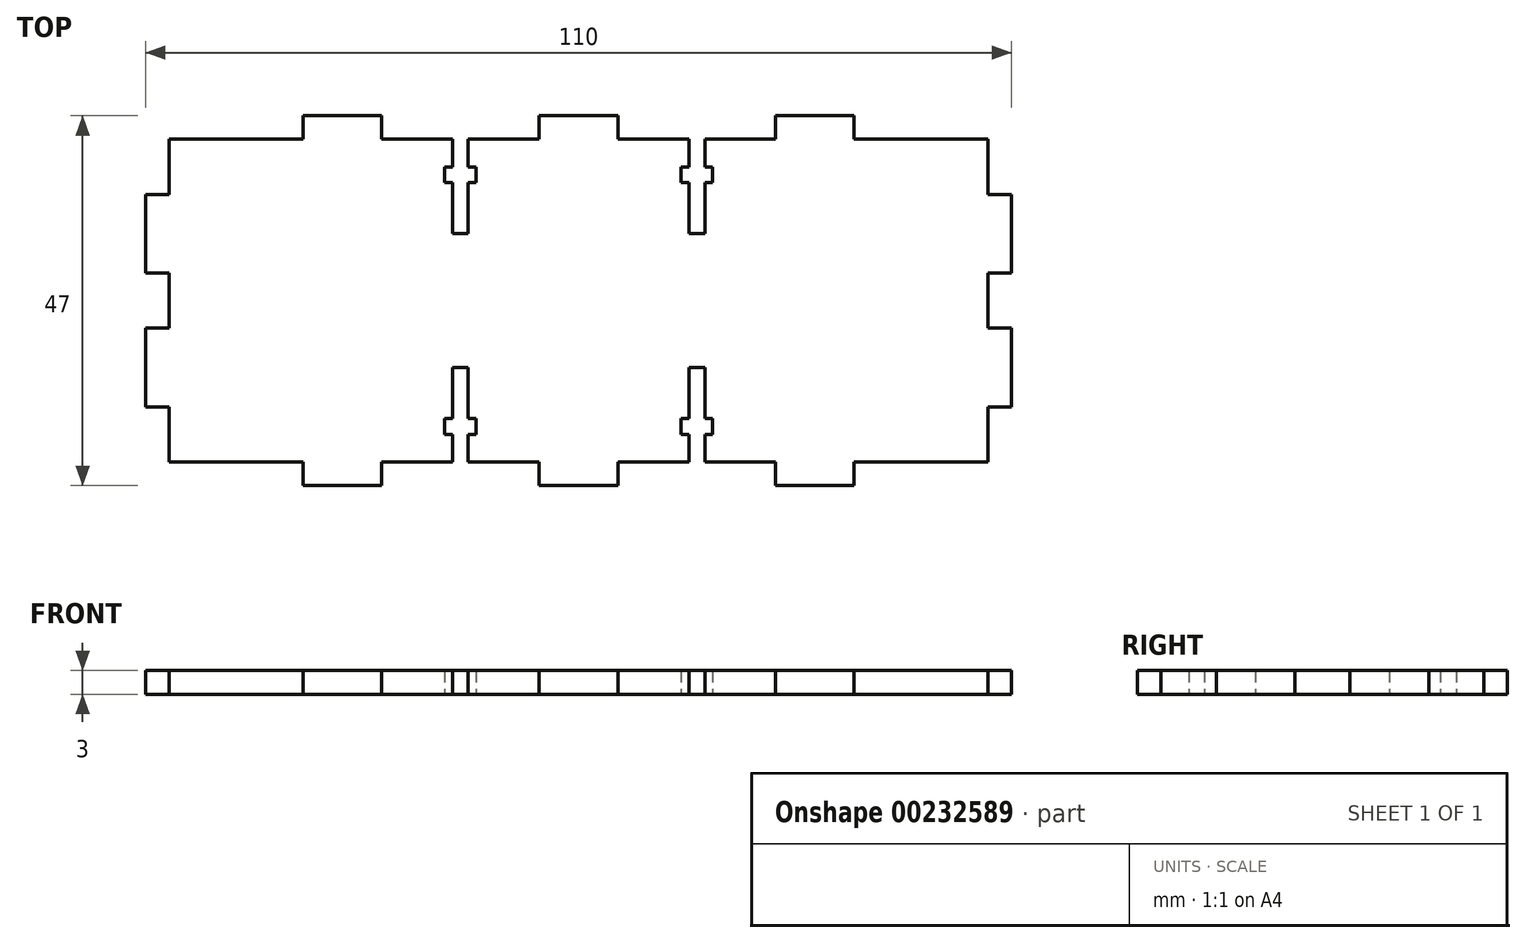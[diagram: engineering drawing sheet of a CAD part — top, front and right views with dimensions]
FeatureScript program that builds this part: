
annotation { "Feature Type Name" : "Feature", "Feature Type Description" : "" }
export const myFeature = defineFeature(function(context is Context, id is Id, definition is map)
    precondition{}
    {
        {
            var Q0;
            Q0=qCreatedBy(makeId("Top.planeOp"),FACE);
            var sketch = newSketch(context, id + "F0", { "sketchPlane" : qUnion([Q0])});
            skLineSegment(sketch, "E0.bottom", {"start": v(-45.2, 13.6) * mm, "end": v(-28.2, 13.6) * mm});
            skLineSegment(sketch, "E0.top", {"start": v(-45.2, -27.4) * mm, "end": v(-28.2, -27.4) * mm});
            skLineSegment(sketch, "E0.left", {"start": v(-45.2, 13.6) * mm, "end": v(-45.2, 6.6) * mm});
            skLineSegment(sketch, "E0.right", {"start": v(58.8, 13.6) * mm, "end": v(58.8, -27.4) * mm});
            skLineSegment(sketch, "E1", {"start": v(-45.2, 6.6) * mm, "end": v(-48.2, 6.6) * mm});
            skLineSegment(sketch, "E2", {"start": v(-48.2, 6.6) * mm, "end": v(-48.2, -3.4) * mm});
            skLineSegment(sketch, "E3", {"start": v(-48.2, -3.4) * mm, "end": v(-45.2, -3.4) * mm});
            skLineSegment(sketch, "E4", {"start": v(-45.2, -3.4) * mm, "end": v(-45.2, -10.4) * mm});
            skLineSegment(sketch, "E5", {"start": v(-45.2, -10.4) * mm, "end": v(-48.2, -10.4) * mm});
            skLineSegment(sketch, "E6", {"start": v(-48.2, -10.4) * mm, "end": v(-48.2, -20.4) * mm});
            skLineSegment(sketch, "E7", {"start": v(-48.2, -20.4) * mm, "end": v(-45.2, -20.4) * mm});
            skLineSegment(sketch, "E8", {"start": v(-45.2, -20.4) * mm, "end": v(-45.2, -27.4) * mm});
            skLineSegment(sketch, "E9", {"start": v(-28.2, 13.6) * mm, "end": v(-28.2, 16.6) * mm});
            skLineSegment(sketch, "E10", {"start": v(-28.2, 16.6) * mm, "end": v(-18.2, 16.6) * mm});
            skLineSegment(sketch, "E11", {"start": v(-18.2, 16.6) * mm, "end": v(-18.2, 13.6) * mm});
            skLineSegment(sketch, "E12", {"start": v(1.8, 16.6) * mm, "end": v(1.8, 13.6) * mm});
            skLineSegment(sketch, "E13", {"start": v(1.8, 16.6) * mm, "end": v(11.8, 16.6) * mm});
            skLineSegment(sketch, "E14", {"start": v(11.8, 16.6) * mm, "end": v(11.8, 13.6) * mm});
            skLineSegment(sketch, "E15", {"start": v(31.8, 16.6) * mm, "end": v(41.8, 16.6) * mm});
            skLineSegment(sketch, "E16", {"start": v(31.8, 16.6) * mm, "end": v(31.8, 13.6) * mm});
            skLineSegment(sketch, "E17", {"start": v(41.8, 16.6) * mm, "end": v(41.8, 13.6) * mm});
            skLineSegment(sketch, "E18.MirrorCS", {"start": v(58.8, 13.6) * mm, "end": v(58.8, 6.6) * mm});
            skLineSegment(sketch, "E19.MirrorCS", {"start": v(61.8, 6.6) * mm, "end": v(61.8, -3.4) * mm});
            skLineSegment(sketch, "E20.MirrorCS", {"start": v(58.8, 6.6) * mm, "end": v(61.8, 6.6) * mm});
            skLineSegment(sketch, "E21.MirrorCS", {"start": v(61.8, -3.4) * mm, "end": v(58.8, -3.4) * mm});
            skLineSegment(sketch, "E22.MirrorCS", {"start": v(58.8, -10.4) * mm, "end": v(61.8, -10.4) * mm});
            skLineSegment(sketch, "E23.MirrorCS", {"start": v(61.8, -10.4) * mm, "end": v(61.8, -20.4) * mm});
            skLineSegment(sketch, "E24.MirrorCS", {"start": v(61.8, -20.4) * mm, "end": v(58.8, -20.4) * mm});
            skLineSegment(sketch, "E25.MirrorCS", {"start": v(-28.2, -27.4) * mm, "end": v(-28.2, -30.4) * mm});
            skLineSegment(sketch, "E26.MirrorCS", {"start": v(-28.2, -30.4) * mm, "end": v(-18.2, -30.4) * mm});
            skLineSegment(sketch, "E27.MirrorCS", {"start": v(-18.2, -30.4) * mm, "end": v(-18.2, -27.4) * mm});
            skLineSegment(sketch, "E28.MirrorCS", {"start": v(1.8, -30.4) * mm, "end": v(1.8, -27.4) * mm});
            skLineSegment(sketch, "E29.MirrorCS", {"start": v(1.8, -30.4) * mm, "end": v(11.8, -30.4) * mm});
            skLineSegment(sketch, "E30.MirrorCS", {"start": v(11.8, -30.4) * mm, "end": v(11.8, -27.4) * mm});
            skLineSegment(sketch, "E31.MirrorCS", {"start": v(31.8, -30.4) * mm, "end": v(41.8, -30.4) * mm});
            skLineSegment(sketch, "E32.MirrorCS", {"start": v(41.8, -30.4) * mm, "end": v(41.8, -27.4) * mm});
            skLineSegment(sketch, "E33.MirrorCS", {"start": v(31.8, -30.4) * mm, "end": v(31.8, -27.4) * mm});
            skLineSegment(sketch, "E34", {"start": v(58.8, -27.4) * mm, "end": v(45.3, -27.4) * mm});
            skLineSegment(sketch, "E35", {"start": v(-18.2, 13.6) * mm, "end": v(-9.22, 13.6) * mm});
            skLineSegment(sketch, "E36", {"start": v(-9.22, 13.6) * mm, "end": v(-9.22, 10.1) * mm});
            skLineSegment(sketch, "E37", {"start": v(-9.22, 10.1) * mm, "end": v(-10.22, 10.1) * mm});
            skLineSegment(sketch, "E38", {"start": v(-10.22, 10.1) * mm, "end": v(-10.22, 8.1) * mm});
            skLineSegment(sketch, "E39", {"start": v(-10.22, 8.1) * mm, "end": v(-9.22, 8.1) * mm});
            skLineSegment(sketch, "E40", {"start": v(-9.22, 8.1) * mm, "end": v(-9.22, 1.6) * mm});
            skLineSegment(sketch, "E41", {"start": v(-9.22, 1.6) * mm, "end": v(-7.22, 1.6) * mm});
            skLineSegment(sketch, "E42", {"start": v(-7.22, 1.6) * mm, "end": v(-7.22, 8.1) * mm});
            skLineSegment(sketch, "E43", {"start": v(-7.22, 8.1) * mm, "end": v(-6.22, 8.1) * mm});
            skLineSegment(sketch, "E44", {"start": v(-6.22, 8.1) * mm, "end": v(-6.22, 10.1) * mm});
            skLineSegment(sketch, "E45", {"start": v(-6.22, 10.1) * mm, "end": v(-7.22, 10.1) * mm});
            skLineSegment(sketch, "E46", {"start": v(-7.22, 10.1) * mm, "end": v(-7.22, 13.6) * mm});
            skLineSegment(sketch, "E47.MirrorCS", {"start": v(20.84, 10.1) * mm, "end": v(20.84, 13.6) * mm});
            skLineSegment(sketch, "E48.MirrorCS", {"start": v(19.84, 10.1) * mm, "end": v(20.84, 10.1) * mm});
            skLineSegment(sketch, "E49.MirrorCS", {"start": v(19.84, 8.1) * mm, "end": v(19.84, 10.1) * mm});
            skLineSegment(sketch, "E50.MirrorCS", {"start": v(20.84, 8.1) * mm, "end": v(19.84, 8.1) * mm});
            skLineSegment(sketch, "E51.MirrorCS", {"start": v(20.84, 1.6) * mm, "end": v(20.84, 8.1) * mm});
            skLineSegment(sketch, "E52.MirrorCS", {"start": v(22.84, 8.1) * mm, "end": v(22.84, 1.6) * mm});
            skLineSegment(sketch, "E53.MirrorCS", {"start": v(23.84, 8.1) * mm, "end": v(22.84, 8.1) * mm});
            skLineSegment(sketch, "E54.MirrorCS", {"start": v(23.84, 10.1) * mm, "end": v(23.84, 8.1) * mm});
            skLineSegment(sketch, "E55.MirrorCS", {"start": v(22.84, 10.1) * mm, "end": v(23.84, 10.1) * mm});
            skLineSegment(sketch, "E56.MirrorCS", {"start": v(22.84, 13.6) * mm, "end": v(22.84, 10.1) * mm});
            skLineSegment(sketch, "E57.MirrorCS", {"start": v(22.84, 1.6) * mm, "end": v(20.84, 1.6) * mm});
            skLineSegment(sketch, "E58.MirrorCS", {"start": v(-9.22, -21.9) * mm, "end": v(-9.22, -15.4) * mm});
            skLineSegment(sketch, "E59.MirrorCS", {"start": v(-9.22, -15.4) * mm, "end": v(-7.22, -15.4) * mm});
            skLineSegment(sketch, "E60.MirrorCS", {"start": v(-7.22, -15.4) * mm, "end": v(-7.22, -21.9) * mm});
            skLineSegment(sketch, "E61.MirrorCS", {"start": v(-7.22, -21.9) * mm, "end": v(-6.22, -21.9) * mm});
            skLineSegment(sketch, "E62.MirrorCS", {"start": v(-6.22, -21.9) * mm, "end": v(-6.22, -23.9) * mm});
            skLineSegment(sketch, "E63.MirrorCS", {"start": v(-10.22, -23.9) * mm, "end": v(-10.22, -21.9) * mm});
            skLineSegment(sketch, "E64.MirrorCS", {"start": v(-10.22, -21.9) * mm, "end": v(-9.22, -21.9) * mm});
            skLineSegment(sketch, "E65.MirrorCS", {"start": v(-9.22, -23.9) * mm, "end": v(-10.22, -23.9) * mm});
            skLineSegment(sketch, "E66.MirrorCS", {"start": v(-9.22, -27.4) * mm, "end": v(-9.22, -23.9) * mm});
            skLineSegment(sketch, "E67.MirrorCS", {"start": v(-7.22, -23.9) * mm, "end": v(-7.22, -27.4) * mm});
            skLineSegment(sketch, "E68.MirrorCS", {"start": v(-6.22, -23.9) * mm, "end": v(-7.22, -23.9) * mm});
            skLineSegment(sketch, "E69.MirrorCS", {"start": v(22.84, -15.4) * mm, "end": v(20.84, -15.4) * mm});
            skLineSegment(sketch, "E70.MirrorCS", {"start": v(20.84, -15.4) * mm, "end": v(20.84, -21.9) * mm});
            skLineSegment(sketch, "E71.MirrorCS", {"start": v(22.84, -21.9) * mm, "end": v(22.84, -15.4) * mm});
            skLineSegment(sketch, "E72.MirrorCS", {"start": v(23.84, -21.9) * mm, "end": v(22.84, -21.9) * mm});
            skLineSegment(sketch, "E73.MirrorCS", {"start": v(23.84, -23.9) * mm, "end": v(23.84, -21.9) * mm});
            skLineSegment(sketch, "E74.MirrorCS", {"start": v(22.84, -23.9) * mm, "end": v(23.84, -23.9) * mm});
            skLineSegment(sketch, "E75.MirrorCS", {"start": v(22.84, -27.4) * mm, "end": v(22.84, -23.9) * mm});
            skLineSegment(sketch, "E76.MirrorCS", {"start": v(20.84, -23.9) * mm, "end": v(20.84, -27.4) * mm});
            skLineSegment(sketch, "E77.MirrorCS", {"start": v(19.84, -23.9) * mm, "end": v(20.84, -23.9) * mm});
            skLineSegment(sketch, "E78.MirrorCS", {"start": v(19.84, -21.9) * mm, "end": v(19.84, -23.9) * mm});
            skLineSegment(sketch, "E79.MirrorCS", {"start": v(20.84, -21.9) * mm, "end": v(19.84, -21.9) * mm});
            skLineSegment(sketch, "E80.trimOffspring", {"start": v(11.8, 13.6) * mm, "end": v(20.84, 13.6) * mm});
            skLineSegment(sketch, "E81.trimOffspring", {"start": v(41.8, 13.6) * mm, "end": v(58.8, 13.6) * mm});
            skLineSegment(sketch, "E82.trimOffspring", {"start": v(22.84, 13.6) * mm, "end": v(31.8, 13.6) * mm});
            skLineSegment(sketch, "E83.trimOffspring", {"start": v(-7.22, 13.6) * mm, "end": v(1.8, 13.6) * mm});
            skLineSegment(sketch, "E84.trimOffspring", {"start": v(-7.22, -27.4) * mm, "end": v(1.8, -27.4) * mm});
            skLineSegment(sketch, "E85.trimOffspring", {"start": v(22.84, -27.4) * mm, "end": v(31.8, -27.4) * mm});
            skLineSegment(sketch, "E86.trimOffspring", {"start": v(41.8, -27.4) * mm, "end": v(58.8, -27.4) * mm});
            skLineSegment(sketch, "E87.trimOffspring", {"start": v(58.8, -20.4) * mm, "end": v(58.8, -27.4) * mm});
            skLineSegment(sketch, "E88.trimOffspring", {"start": v(58.8, -3.4) * mm, "end": v(58.8, -10.4) * mm});
            skLineSegment(sketch, "E89.trimOffspring", {"start": v(-18.2, -27.4) * mm, "end": v(-9.22, -27.4) * mm});
            skLineSegment(sketch, "E90.trimOffspring", {"start": v(11.8, -27.4) * mm, "end": v(20.84, -27.4) * mm});
            skSolve(sketch);
        }
        {
            var Q0;
            Q0 = qSketchRegion(id + "F0", true);
            extrude(context, id + "F1", {"entities" : qUnion([Q0]), "depth" : 3 * mm});
        }
    });
